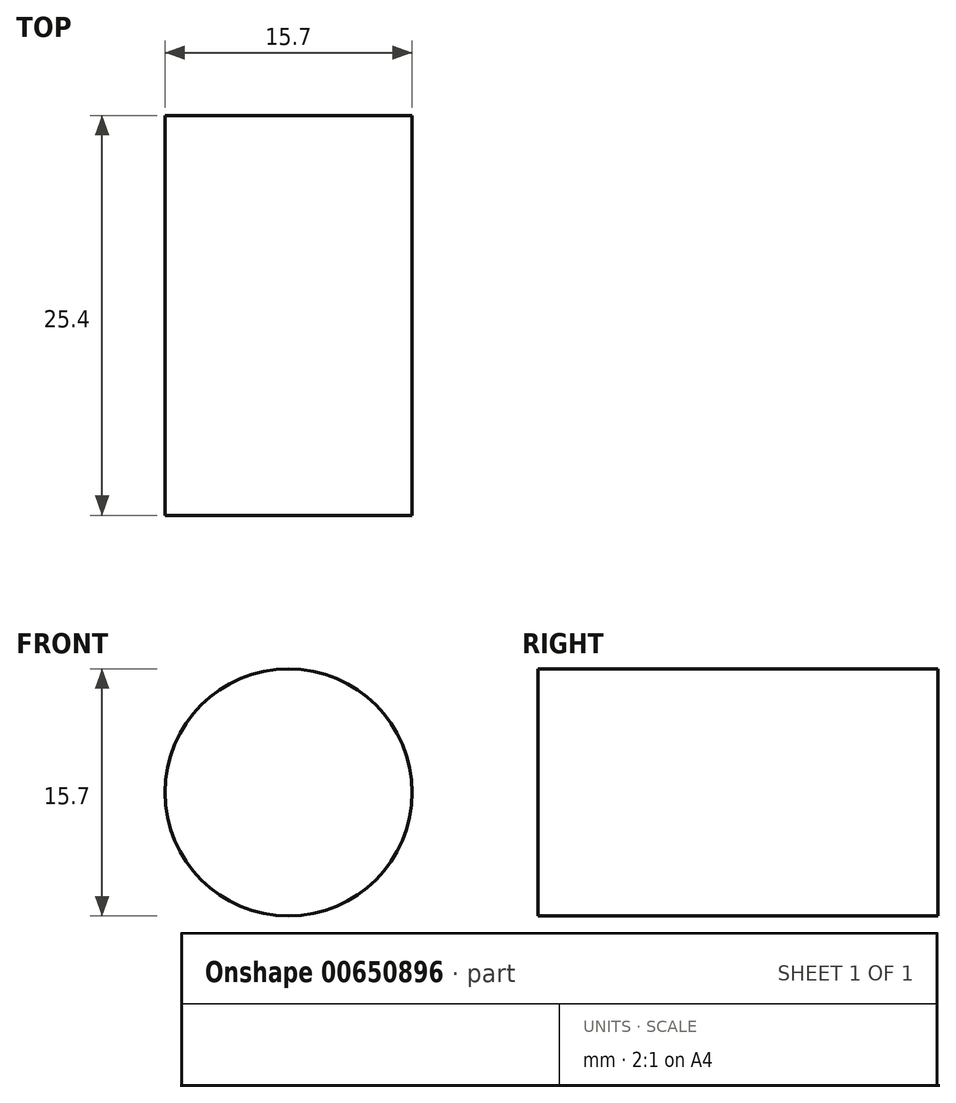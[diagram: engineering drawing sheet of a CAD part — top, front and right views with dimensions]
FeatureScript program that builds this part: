
annotation { "Feature Type Name" : "Feature", "Feature Type Description" : "" }
export const myFeature = defineFeature(function(context is Context, id is Id, definition is map)
    precondition{}
    {
        {
            var Q0;
            Q0=qCreatedBy(makeId("Front.planeOp"),FACE);
            var sketch = newSketch(context, id + "F0", { "sketchPlane" : qUnion([Q0])});
            skCircle(sketch, "E0", {"center": v(0, 0) * mm, "radius": 7.85 * mm});
            skSolve(sketch);
        }
        {
            var Q0;
            Q0=sQuery(id+"F0.wireOp",EDGE,"E0");
            extrude(context, id + "F1", {"bodyType" : ToolBodyType.SURFACE, "surfaceEntities" : qUnion([Q0]), "depth" : 25.4 * mm, "offsetDistance" : 25 * mm});
        }
    });
